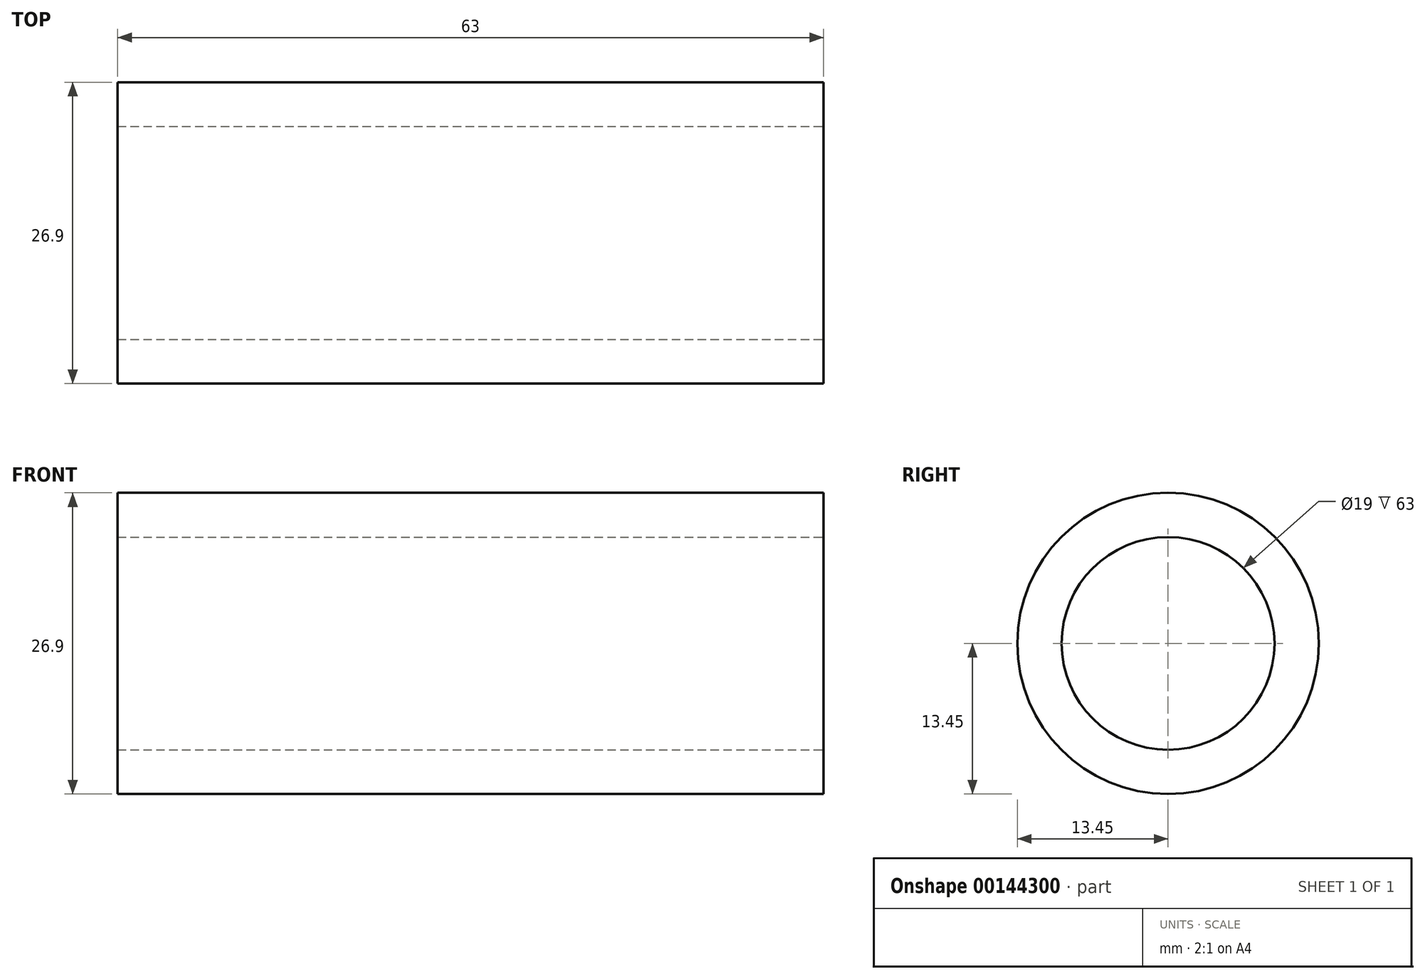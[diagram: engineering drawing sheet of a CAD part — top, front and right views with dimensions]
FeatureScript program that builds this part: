
annotation { "Feature Type Name" : "Feature", "Feature Type Description" : "" }
export const myFeature = defineFeature(function(context is Context, id is Id, definition is map)
    precondition{}
    {
        {
            var Q0;
            Q0=qCreatedBy(makeId("Right.planeOp"),FACE);
            var sketch = newSketch(context, id + "F0", { "sketchPlane" : qUnion([Q0])});
            skCircle(sketch, "E0", {"center": v(0, 0) * mm, "radius": 13.45 * mm});
            skCircle(sketch, "E1", {"center": v(0, 0) * mm, "radius": 9.5 * mm});
            skSolve(sketch);
        }
        {
            var Q0;
            Q0 = qSketchRegion(id + "F0", true);
            extrude(context, id + "F1", {"entities" : qUnion([Q0]), "oppositeDirection" : true, "depth" : 63 * mm});
        }
    });
